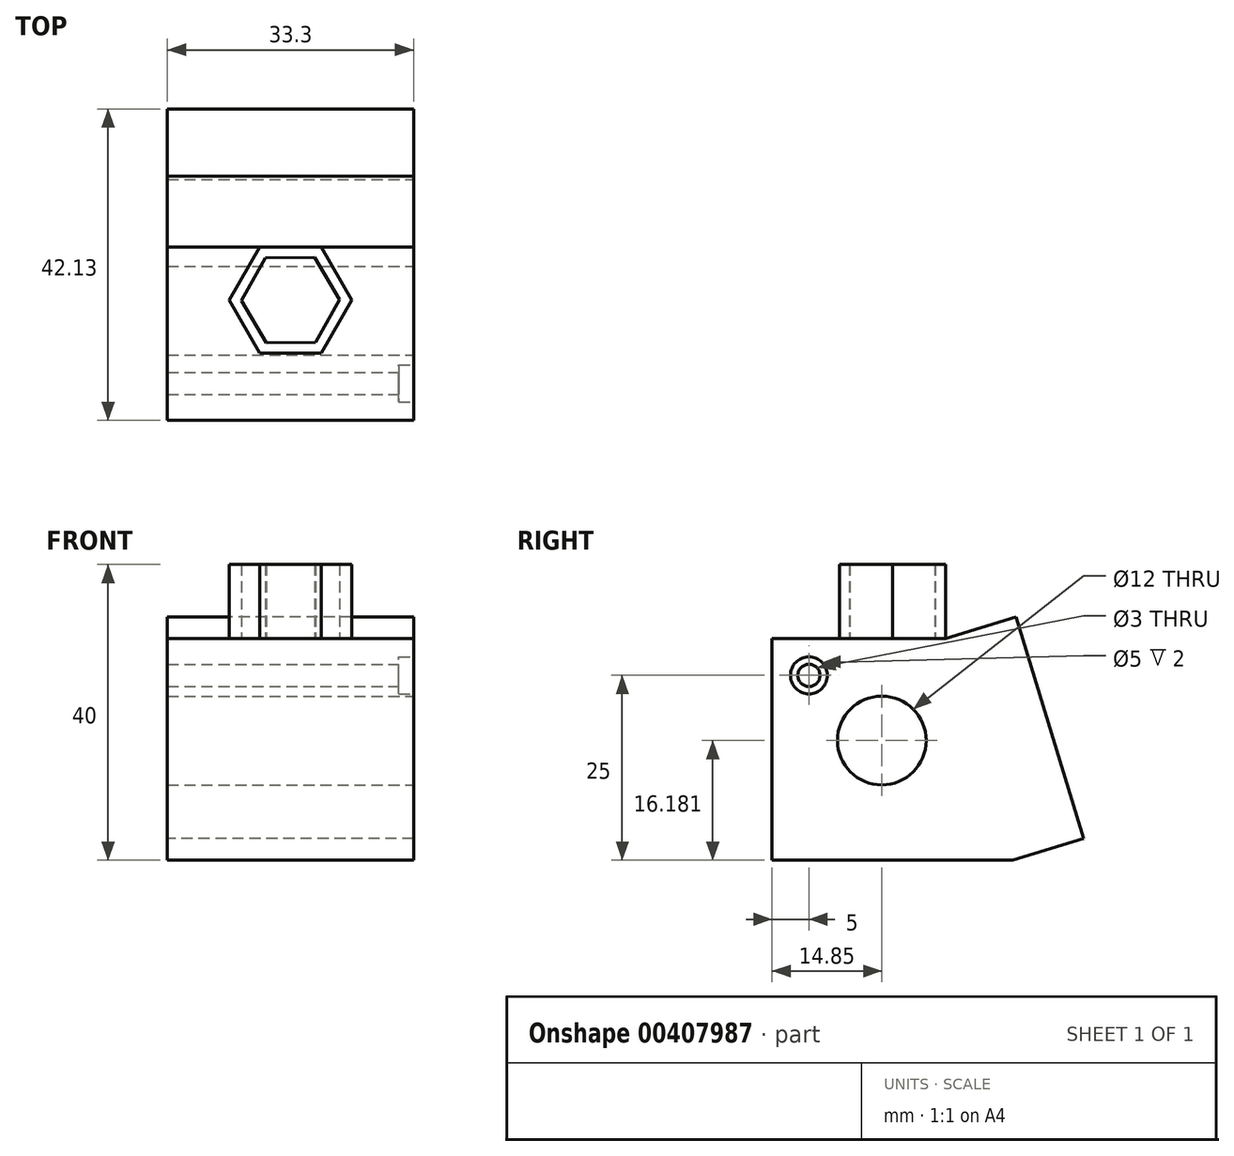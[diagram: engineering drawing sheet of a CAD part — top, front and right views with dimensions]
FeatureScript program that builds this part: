
annotation { "Feature Type Name" : "Feature", "Feature Type Description" : "" }
export const myFeature = defineFeature(function(context is Context, id is Id, definition is map)
    precondition{}
    {
        {
            var Q0;
            Q0=qCreatedBy(makeId("Top.planeOp"),FACE);
            var sketch = newSketch(context, id + "F0", { "sketchPlane" : qUnion([Q0])});
            skLineSegment(sketch, "E0.bottom", {"start": v(-27.83, 7.18) * mm, "end": v(5.47, 7.18) * mm});
            skLineSegment(sketch, "E0.top", {"start": v(-27.83, -25.38) * mm, "end": v(5.47, -25.38) * mm});
            skLineSegment(sketch, "E0.left", {"start": v(-27.83, 7.18) * mm, "end": v(-27.83, -25.38) * mm});
            skLineSegment(sketch, "E0.right", {"start": v(5.47, 7.18) * mm, "end": v(5.47, -25.38) * mm});
            skSolve(sketch);
        }
        {
            var Q0;
            Q0 = qSketchRegion(id + "F0", true);
            extrude(context, id + "F1", {"entities" : qUnion([Q0]), "depth" : 30 * mm});
        }
        {
            var Q0;
            Q0=makeQuery(id+"F1.opExtrude","CAP_FACE",FACE,{"disambiguationData":[OSD([sQuery(id+"F0.wireOp",EDGE,"E0.bottom"),sQuery(id+"F0.wireOp",EDGE,"E0.top"),sQuery(id+"F0.wireOp",EDGE,"E0.left"),sQuery(id+"F0.wireOp",EDGE,"E0.right")])],"isStart":false});
            var sketch = newSketch(context, id + "F2", { "sketchPlane" : qUnion([Q0])});
            skCircle(sketch, "E1.cCircle", {"center": v(-11.18, -9.1) * mm, "radius": 7.18 * mm, "construction": true});
            skLineSegment(sketch, "E1.0", {"start": v(-7.04, -16.28) * mm, "end": v(-15.32, -16.28) * mm});
            skLineSegment(sketch, "E1.1", {"start": v(-15.32, -16.28) * mm, "end": v(-19.47, -9.1) * mm});
            skLineSegment(sketch, "E1.2", {"start": v(-19.47, -9.1) * mm, "end": v(-15.32, -1.93) * mm});
            skLineSegment(sketch, "E1.3", {"start": v(-15.32, -1.93) * mm, "end": v(-7.04, -1.93) * mm});
            skLineSegment(sketch, "E1.4", {"start": v(-7.04, -1.93) * mm, "end": v(-2.9, -9.1) * mm});
            skLineSegment(sketch, "E1.5", {"start": v(-2.9, -9.1) * mm, "end": v(-7.04, -16.28) * mm});
            skPoint(sketch, "E1.0.midPoint", {"position": v(-11.18, -16.28) * mm});
            skCircle(sketch, "E2.cCircle", {"center": v(-11.18, -9.1) * mm, "radius": 5.75 * mm, "construction": true});
            skLineSegment(sketch, "E2.0", {"start": v(-17.82, -9.16) * mm, "end": v(-14.55, -3.38) * mm});
            skLineSegment(sketch, "E2.1", {"start": v(-14.55, -3.38) * mm, "end": v(-7.91, -3.32) * mm});
            skLineSegment(sketch, "E2.2", {"start": v(-7.91, -3.32) * mm, "end": v(-4.54, -9.04) * mm});
            skLineSegment(sketch, "E2.3", {"start": v(-4.54, -9.04) * mm, "end": v(-7.81, -14.82) * mm});
            skLineSegment(sketch, "E2.4", {"start": v(-7.81, -14.82) * mm, "end": v(-14.45, -14.88) * mm});
            skLineSegment(sketch, "E2.5", {"start": v(-14.45, -14.88) * mm, "end": v(-17.82, -9.16) * mm});
            skPoint(sketch, "E2.0.midPoint", {"position": v(-16.19, -6.27) * mm});
            skSolve(sketch);
        }
        {
            var Q0;
            Q0=makeQuery(id+"F2.imprint","IMPRINT",FACE,{"disambiguationData":[TD([[makeQuery(id+"F2.imprint","IMPRINT",EDGE,{"derivedFrom":sQuery(id+"F2.wireOp",EDGE,"E1.0")}),-1.0]])]});
            extrude(context, id + "F3", {"entities" : qUnion([Q0]), "operationType" : NewBodyOperationType.ADD, "depth" : 10 * mm});
        }
        {
            var Q0;
            Q0=makeQuery(id+"F1.opExtrude","SWEPT_FACE",FACE,{"disambiguationData":[OSD([sQuery(id+"F0.wireOp",EDGE,"E0.right")])]});
            var sketch = newSketch(context, id + "F4", { "sketchPlane" : qUnion([Q0])});
            skPoint(sketch, "E3", {"position": v(-10.53, 16.18) * mm});
            skPoint(sketch, "E4", {"position": v(-20.38, 25) * mm});
            skSolve(sketch);
        }
        {
            var Q0;
            Q0=sQuery(id+"F4.wireOp",VERTEX,"E3");
            var Q1;
            Q1=makeQuery(id+"F1.opExtrude","SWEPT_BODY",BODY,{"disambiguationData":[OSD([sQuery(id+"F0.wireOp",EDGE,"E0.bottom"),sQuery(id+"F0.wireOp",EDGE,"E0.top"),sQuery(id+"F0.wireOp",EDGE,"E0.left"),sQuery(id+"F0.wireOp",EDGE,"E0.right")])]});
            hole(context, id + "F5", {"style" : HoleStyle.SIMPLE, "endStyle" : HoleEndStyle.THROUGH, "holeDiameter" : 12 * mm, "isTappedThrough" : true, "tappedDepth" : 12 * mm, "tapClearance" : 3, "locations" : qUnion([Q0]), "scope" : qUnion([Q1])});
        }
        {
            var Q0;
            Q0=sQuery(id+"F4.wireOp",VERTEX,"E4");
            var Q1;
            Q1=makeQuery(id+"F1.opExtrude","SWEPT_BODY",BODY,{"disambiguationData":[OSD([sQuery(id+"F0.wireOp",EDGE,"E0.bottom"),sQuery(id+"F0.wireOp",EDGE,"E0.top"),sQuery(id+"F0.wireOp",EDGE,"E0.left"),sQuery(id+"F0.wireOp",EDGE,"E0.right")])]});
            hole(context, id + "F6", {"style" : HoleStyle.C_BORE, "endStyle" : HoleEndStyle.THROUGH, "holeDiameter" : 3 * mm, "cBoreDiameter" : 5 * mm, "cBoreDepth" : 2 * mm, "isTappedThrough" : true, "tappedDepth" : 12 * mm, "tapClearance" : 3, "locations" : qUnion([Q0]), "scope" : qUnion([Q1])});
        }
        {
            var Q0;
            Q0=makeQuery(id+"F1.opExtrude","CAP_VERTEX",VERTEX,{"disambiguationData":[OSD([sQuery(id+"F0.wireOp",EDGE,"E0.bottom"),sQuery(id+"F0.wireOp",EDGE,"E0.right")])],"isStart":true});
            var Q1;
            Q1=makeQuery(id+"F1.opExtrude","CAP_VERTEX",VERTEX,{"disambiguationData":[OSD([sQuery(id+"F0.wireOp",EDGE,"E0.bottom"),sQuery(id+"F0.wireOp",EDGE,"E0.left")])],"isStart":true});
            var Q2;
            Q2=sQuery(id+"F2.wireOp",VERTEX,"E1.3.start");
            cPlane(context, id + "F7", {"entities" : qUnion([Q0, Q1, Q2]), "cplaneType" : CPlaneType.THREE_POINT, "offset" : 1 * mm, "width" : 150 * mm, "height" : 150 * mm});
        }
        {
            var Q0;
            Q0=qCreatedBy(id+"F7.planeOp",FACE);
            var sketch = newSketch(context, id + "F8", { "sketchPlane" : qUnion([Q0])});
            skLineSegment(sketch, "E5.bottom", {"start": v(5.47, -2.08) * mm, "end": v(-27.83, -2.08) * mm});
            skLineSegment(sketch, "E5.top", {"start": v(5.47, 29.27) * mm, "end": v(-27.83, 29.27) * mm});
            skLineSegment(sketch, "E5.left", {"start": v(5.47, -2.08) * mm, "end": v(5.47, 29.27) * mm});
            skLineSegment(sketch, "E5.right", {"start": v(-27.83, -2.08) * mm, "end": v(-27.83, 29.27) * mm});
            skSolve(sketch);
        }
        {
            var Q0;
            Q0 = qSketchRegion(id + "F8", true);
            extrude(context, id + "F9", {"entities" : qUnion([Q0]), "operationType" : NewBodyOperationType.ADD, "depth" : -10 * mm});
        }
    });
